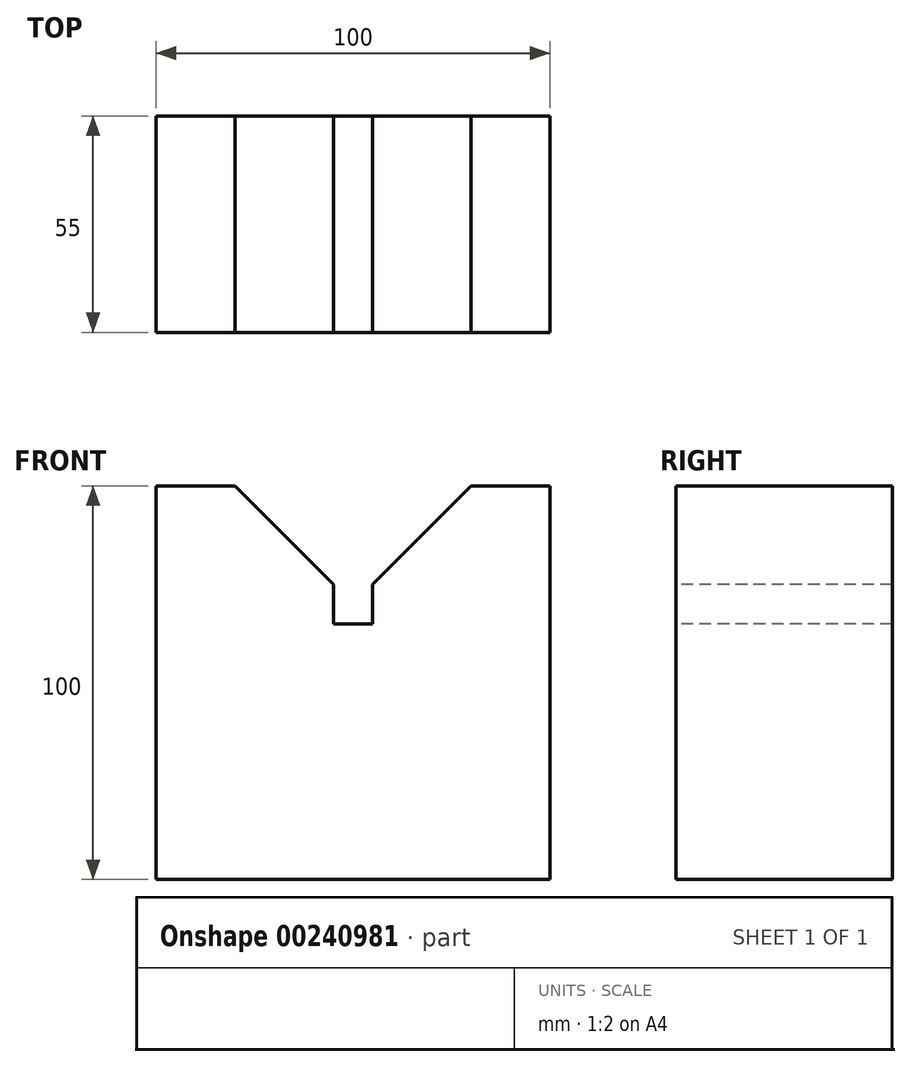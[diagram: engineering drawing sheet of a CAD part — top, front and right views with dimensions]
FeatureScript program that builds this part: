
annotation { "Feature Type Name" : "Feature", "Feature Type Description" : "" }
export const myFeature = defineFeature(function(context is Context, id is Id, definition is map)
    precondition{}
    {
        {
            var Q0;
            Q0=qCreatedBy(makeId("Front.planeOp"),FACE);
            var sketch = newSketch(context, id + "F0", { "sketchPlane" : qUnion([Q0])});
            skLineSegment(sketch, "E0", {"start": v(-50, 0) * mm, "end": v(50, 0) * mm});
            skLineSegment(sketch, "E1", {"start": v(50, 0) * mm, "end": v(50, 100) * mm});
            skLineSegment(sketch, "E2", {"start": v(50, 100) * mm, "end": v(30, 100) * mm});
            skLineSegment(sketch, "E3", {"start": v(30, 100) * mm, "end": v(5, 75) * mm});
            skLineSegment(sketch, "E4", {"start": v(5, 75) * mm, "end": v(5, 65) * mm});
            skLineSegment(sketch, "E5", {"start": v(5, 65) * mm, "end": v(-5, 65) * mm});
            skLineSegment(sketch, "E6", {"start": v(-5, 65) * mm, "end": v(-5, 75) * mm});
            skLineSegment(sketch, "E7", {"start": v(-5, 75) * mm, "end": v(-30, 100) * mm});
            skLineSegment(sketch, "E8", {"start": v(-30, 100) * mm, "end": v(-50, 100) * mm});
            skLineSegment(sketch, "E9", {"start": v(-50, 100) * mm, "end": v(-50, 0) * mm});
            skSolve(sketch);
        }
        {
            var Q0;
            Q0 = qSketchRegion(id + "F0", true);
            extrude(context, id + "F1", {"entities" : qUnion([Q0]), "oppositeDirection" : true, "depth" : 55 * mm});
        }
    });
